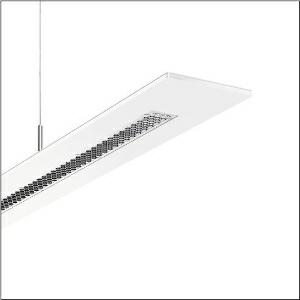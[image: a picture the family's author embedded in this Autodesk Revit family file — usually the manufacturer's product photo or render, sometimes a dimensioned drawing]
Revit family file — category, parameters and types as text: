
# Revit family: arktika_r__21_5mb2512l30830_74ae
name_source: partatom
category: Lighting Fixtures
units: mm (PartAtom-declared; Revit-internal decimal feet)

## family parameters
Cut with Voids When Loaded = No
Host = Face
Light Source = No
Part Type = Normal
Room Calculation Point = No
Round Connector Dimension = Use Diameter
Shared = No

## types (1)
- Arktika® 21 (1 x LED 3000K / CRI = 80 (unbekannt), 3670 lm, 3000K)
    Apparent Load = 31 VA
    CIE Flux Codes = 81 100 100 79 100
    Color Rendering = 80
    Color Temperature = 3000K
    Default Elevation = 1800 mm
    Description = Arktika® 21, office luminaire, primary anti-glare with honeycomb louvre, of plastic, aluminium vaporised, highly specular, light emission: direct/indirect distribution, primary light characteristic: symmetric, installation type: suspended mounting, LED, rated luminous flux: 3.670lm, luminous efficacy: 120lm/W, light colour: 830, colour temperature: 3000K, control gear: ON/OFF, with terminal, 3-pole, mains connection: 220..240V, AC, 50/60Hz, rated input power: 31W, housing, of aluminium, powder-coated, traffic white (RAL 9016), 1-length, length: 1.250mm, width: 120mm, height: 8mm, protection rating (complete): IP20, insulation class (complete): insulation class II (safety insulation), certification: CE, packaging unit: 1 piece
    Height = 8 mm  [stored 0.0262467 ft]
    Lamp = 1 x LED 3000K / CRI >= 80 (unbekannt)
    Lamp Light Flux = 3670 lm
    Lamp count = 1
    Length = 1250 mm
    Luminous efficacy = 120 lm/W
    Manufacturer = Siteco
    ModVariant = No
    Model = 5MB2512L30830
    Mounting Place = Ceiling
    Mounting Type = Pendant
    Number of Poles = 1
    OnlyDefault = Yes
    Power Factor = 1
    Product Name = Arktika® 21
    Product group = office luminaire | ceiling pendant
    ProductGroupID = 903
    Protection Class = Protection class II
    Protection Degree = IP 20
    RLX_Detail_Level = 1
    RLX_Emergency_Light_Flux = 0 lm
    RLX_Emergency_Type = 0
    RLX_Emergency_Type_DB = No
    RlxData = <blob elided: 36061 chars, md5=80105c43>
    Socket = socket
    Standby Power = 0 W
    System Light Flux = 3670 lm
    System Power = 31 W
    Type Comments = Product without accessories
    Type Image = l_1006128.jpg
    URL = http://relux.com
    VarID = ---
    Voltage = 0 V
    Weight = 0.00 kg
    Width = 120 mm

note: [stored X ft] marks values corroborated as IEEE doubles in the binary element streams (Revit-internal decimal feet)

## geometry (parser evidence)
native form markers: Blend x4, Sweep x11
no freeform markers — native parametric forms only
